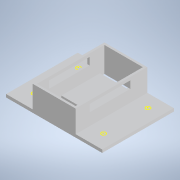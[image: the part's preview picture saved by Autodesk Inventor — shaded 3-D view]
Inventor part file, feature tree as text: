
AUTODESK INVENTOR PART (.ipt)
format: ipt  version: 2021 (Build 250183000, 183)  size: 192,512 bytes
history: native  units: mm
features: sketch x7, extrude x7, reference x4, other x4, projected_geometry x2, plane x1
ambient origin geometry x8: Origin, YZ Plane, XZ Plane, XY Plane, X Axis, Y Axis, Z Axis, Center Point
bodies: Solid1 (feature_tree)
feature tree (25):
  sketch  "Sketch1"  dims[d0=26.0mm d1=45.5mm]
  extrude  "Extrusion1"  Depth=45.5mm
  extrude  "Extrusion2"  Depth=1.5mm
  extrude  "Extrusion3"  Depth=15.0mm TaperAngle=0.0deg
  sketch  "Sketch5"  dims[d13=15.0mm d14=0.0mm d15=3.0mm]
  plane  "Work Plane1"
  extrude  "Extrusion4"  Depth=3.0mm
  extrude  "Extrusion5"  Depth=2.0mm TaperAngle=0.0deg
  extrude  "Extrusion6"  Depth=2.0mm
  extrude  "Extrusion7"  Depth=18.0mm TaperAngle=0.0deg
  sketch  "Sketch2"  dims[d3=1.5mm d4=1.5mm]
  sketch  "Sketch3"  dims[d5=1.5mm d6=15.0mm d7=0.0mm]
  projected_geometry  "Projected Loop1"
  sketch  "Sketch6"  dims[d16=3.0mm d17=2.0mm d18=0.0mm]
  sketch  "Sketch7"  dims[d19=2.0mm d20=0.0mm d21=2.0mm]
  projected_geometry  "Projected Loop2"
  sketch  "Sketch8"  dims[d22=18.0mm d23=0.0mm d24=18.0mm d25=0.0mm d26=9.932mm d27=9.534mm d28=10.0mm d29=0.0mm]
  reference  "Reference1"
  reference  "Reference2"
  reference  "Reference3"
  reference  "Reference4"
  parser-record x1  (decoder bookkeeping rows leaked as tree rows — omitted from the tree; the rows remain in map.json)
  other  "assembly.iam"
  other  "DIN_mount:18"
  other  "DIN_mount:19"
note: 1 file-system path scrubbed to <path> (originals preserved in map.json)
